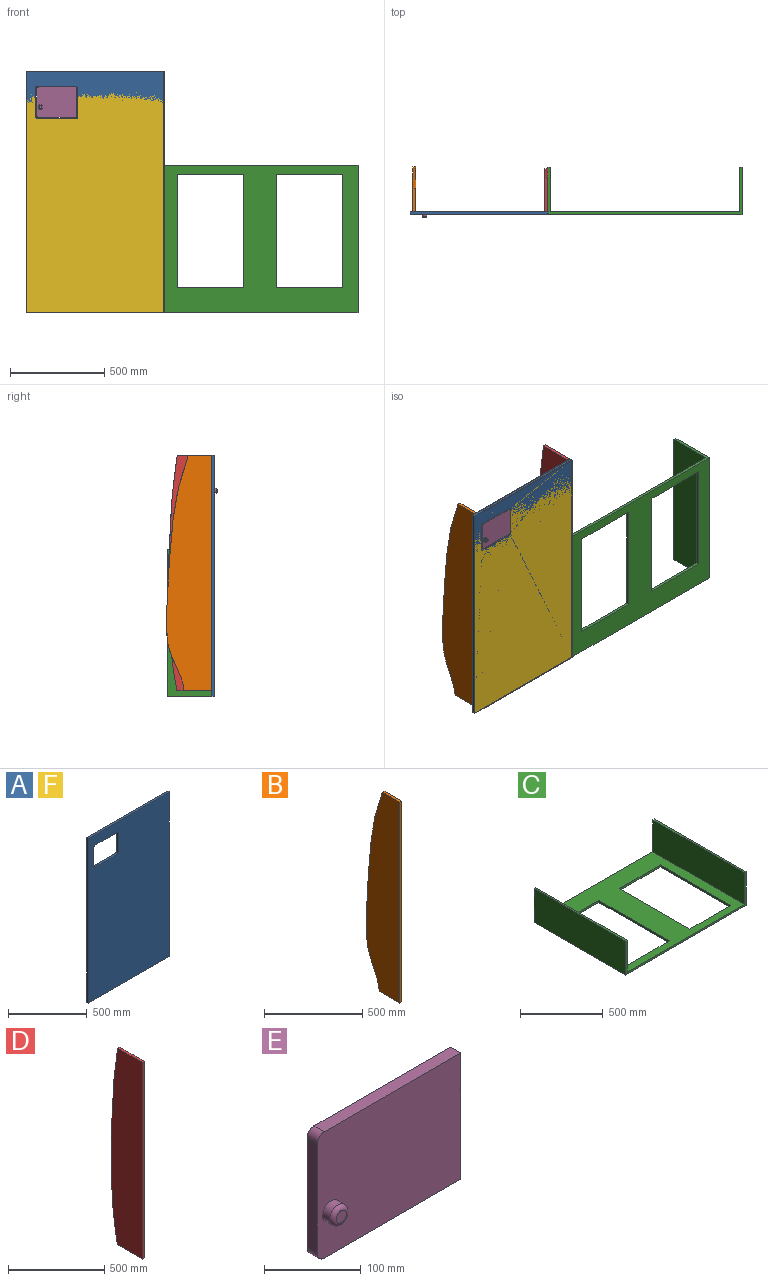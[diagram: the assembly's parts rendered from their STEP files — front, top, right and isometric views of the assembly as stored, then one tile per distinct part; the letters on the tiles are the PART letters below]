
ASSEMBLY  parts=6 mates=10
PART A: 14 faces, bbox 730x15x1280 mm
  f0: plane 1280x15mm, normal (-1,0,0), area 19200mm2, adj f1,f3,f4,f5
  f1: plane 730x15mm, normal (0,0,-1), area 10950mm2, adj f0,f2,f4,f5
  f2: plane 1280x15mm, normal (1,0,0), area 19200mm2, adj f1,f3,f4,f5
  f3: plane 730x15mm, normal (0,0,1), area 10950mm2, adj f0,f2,f4,f5
  f4: plane 1280x730mm, normal (0,-1,0), area 897085.8mm2, adj f0,f1,f2,f3,f6,f7,f8,f9
  f5: plane 1280x730mm, normal (0,1,0), area 897085.8mm2, adj f0,f1,f2,f3,f6,f7,f8,f9
  f6: cylinder r=10mm len=15mm, axis (0,-1,0), area 235.6mm2, adj f4,f5,f7,f13
  f7: plane 200x15mm, normal (0,0,1), area 3000mm2, adj f4,f5,f6,f8
  f8: cylinder r=10mm len=15mm, axis (0,-1,0), area 235.6mm2, adj f4,f5,f7,f9
  f9: plane 150x15mm, normal (1,0,0), area 2250mm2, adj f4,f5,f8,f10
  f10: cylinder r=10mm len=15mm, axis (0,-1,0), area 235.6mm2, adj f4,f5,f9,f11
  f11: plane 200x15mm, normal (0,0,-1), area 3000mm2, adj f4,f5,f10,f12
  f12: cylinder r=10mm len=15mm, axis (0,-1,0), area 235.6mm2, adj f4,f5,f11,f13
  f13: plane 150x15mm, normal (-1,0,0), area 2250mm2, adj f4,f5,f6,f12
PART B: 6 faces, bbox 15x243.5x1250 mm
  f0: plane 146.65x15mm, normal (0,0,-1), area 2199.8mm2, adj f2,f3,f4,f5
  f1: plane 124.7x15mm, normal (0,0,1), area 1870.5mm2, adj f2,f3,f4,f5
  f2: plane 1250x243.47mm, normal (1,0,0), area 256072.3mm2, adj f0,f1,f3,f5
  f3: plane 1250x15mm, normal (0,-1,0), area 18750mm2, adj f0,f1,f2,f4
  f4: plane 1250x243.47mm, normal (-1,0,0), area 256072.3mm2, adj f0,f1,f3,f5
  f5: extruded ~1250x115.34mm, area 19160.1mm2, adj f0,f1,f2,f4
PART C: 18 faces, bbox 1030x780x250 mm
  f0: plane 1030x780mm, normal (0,0,-1), area 383400mm2, adj f2,f3,f8,f9,f10,f11,f12,f13
  f1: plane 1000x780mm, normal (0,0,1), area 360000mm2, adj f5,f6,f8,f9,f10,f11,f12,f13
  f2: plane 780x250mm, normal (-1,0,0), area 195000mm2, adj f0,f7,f8,f9
  f3: plane 780x250mm, normal (1,0,0), area 195000mm2, adj f0,f4,f8,f9
  f4: plane 780x15mm, normal (0,0,1), area 11700mm2, adj f3,f5,f8,f9
  f5: plane 780x235mm, normal (-1,0,0), area 183300mm2, adj f1,f4,f8,f9
  f6: plane 780x235mm, normal (1,0,0), area 183300mm2, adj f1,f7,f8,f9
  f7: plane 780x15mm, normal (0,0,1), area 11700mm2, adj f2,f6,f8,f9
  f8: plane 1030x250mm, normal (0,-1,0), area 22500mm2, adj f0,f1,f2,f3,f4,f5,f6,f7
  f9: plane 1030x250mm, normal (0,1,0), area 22500mm2, adj f0,f1,f2,f3,f4,f5,f6,f7
  f10: plane 350x15mm, normal (0,1,0), area 5250mm2, adj f0,f1,f11,f13
  f11: plane 600x15mm, normal (1,0,0), area 9000mm2, adj f0,f1,f10,f12
  f12: plane 350x15mm, normal (0,-1,0), area 5250mm2, adj f0,f1,f11,f13
  f13: plane 600x15mm, normal (-1,0,0), area 9000mm2, adj f0,f1,f10,f12
  f14: plane 350x15mm, normal (0,1,0), area 5250mm2, adj f0,f1,f15,f17
  f15: plane 600x15mm, normal (1,0,0), area 9000mm2, adj f0,f1,f14,f16
  f16: plane 350x15mm, normal (0,-1,0), area 5250mm2, adj f0,f1,f15,f17
  f17: plane 600x15mm, normal (-1,0,0), area 9000mm2, adj f0,f1,f14,f16
PART D: 6 faces, bbox 15x237.3x1250 mm
  f0: plane 185.16x15mm, normal (0,0,-1), area 2777.4mm2, adj f2,f3,f4,f5
  f1: plane 183.47x15mm, normal (0,0,1), area 2752.1mm2, adj f2,f3,f4,f5
  f2: plane 1250x237.31mm, normal (1,0,0), area 270195.9mm2, adj f0,f1,f3,f5
  f3: plane 1250x15mm, normal (0,-1,0), area 18750mm2, adj f0,f1,f2,f4
  f4: plane 1250x237.31mm, normal (-1,0,0), area 270195.9mm2, adj f0,f1,f3,f5
  f5: extruded ~1250x46.63mm, area 18826mm2, adj f0,f1,f2,f4
PART E: 11 faces, bbox 210x30x160 mm
  f0: plane 210x160mm, normal (0,1,0), area 33557.1mm2, adj f1,f2,f3,f4,f5,f6
  f1: plane 200x15mm, normal (0,0,1), area 3000mm2, adj f0,f2,f6,f7
  f2: plane 160x15mm, normal (1,0,0), area 2400mm2, adj f0,f1,f3,f7
  f3: plane 200x15mm, normal (0,0,-1), area 3000mm2, adj f0,f2,f4,f7
  f4: cylinder r=10mm len=15mm, axis (0,-1,0), area 235.6mm2, adj f0,f3,f5,f7
  f5: plane 140x15mm, normal (-1,0,0), area 2100mm2, adj f0,f4,f6,f7
  f6: cylinder r=10mm len=15mm, axis (0,-1,0), area 235.6mm2, adj f0,f1,f5,f7
  f7: plane 210x160mm, normal (0,-1,0), area 33066.2mm2, adj f1,f2,f3,f4,f5,f6,f8
  f8: cylinder r=12.5mm len=25mm, axis (0,1,0), area 785.4mm2, adj f7,f10
  f9: plane 15x15mm, normal (0,-1,0), area 176.7mm2, adj f10
  f10: torus R=7.5mm, axis (0,-1,0), area 527.2mm2, adj f8,f9
PART F: same geometry as A
PLACE A t=(94.46,-335.34,471.69)mm
PLACE B t=(124.46,14.66,501.69)mm
PLACE C rot(axis=(-1,0,0),90deg) t=(1040.17,-282.81,471.41)mm
PLACE D t=(824.46,64.66,501.69)mm
PLACE E t=(96.28,-335.34,471.94)mm
PLACE F t=(97.46,-335.34,468.86)mm
MATE parallel E.f7 <-> A.f4  axis (0,-1,0) through (257.68,-350.34,1587.31)mm
MATE parallel D.f1 <-> A.f3  axis (0,0,1) through (816.96,-243.6,1751.69)mm
MATE parallel B.f4 <-> A.f0  axis (-1,0,0) through (109.46,-230.39,1106.46)mm
MATE parallel F.f4 <-> A.f4  axis (0,-1,0) through (470.98,-350.34,1089.1)mm
MATE parallel D.f2 <-> A.f2  axis (1,0,0) through (824.46,-226.83,1122.85)mm
MATE parallel A.f5 <-> D.f3  axis (0,1,0) through (824.46,-335.34,1111.69)mm
MATE parallel A.f4 <-> C.f0  axis (0,-1,0) through (467.99,-350.34,1091.94)mm
MATE parallel A.f3 <-> B.f1  axis (0,0,1) through (459.46,-342.84,1751.69)mm
MATE parallel A.f5 <-> B.f3  axis (0,1,0) through (254.59,-335.34,1586.69)mm
MATE parallel C.f2 <-> D.f2  axis (-1,0,0) through (824.46,-225.34,861.41)mm
